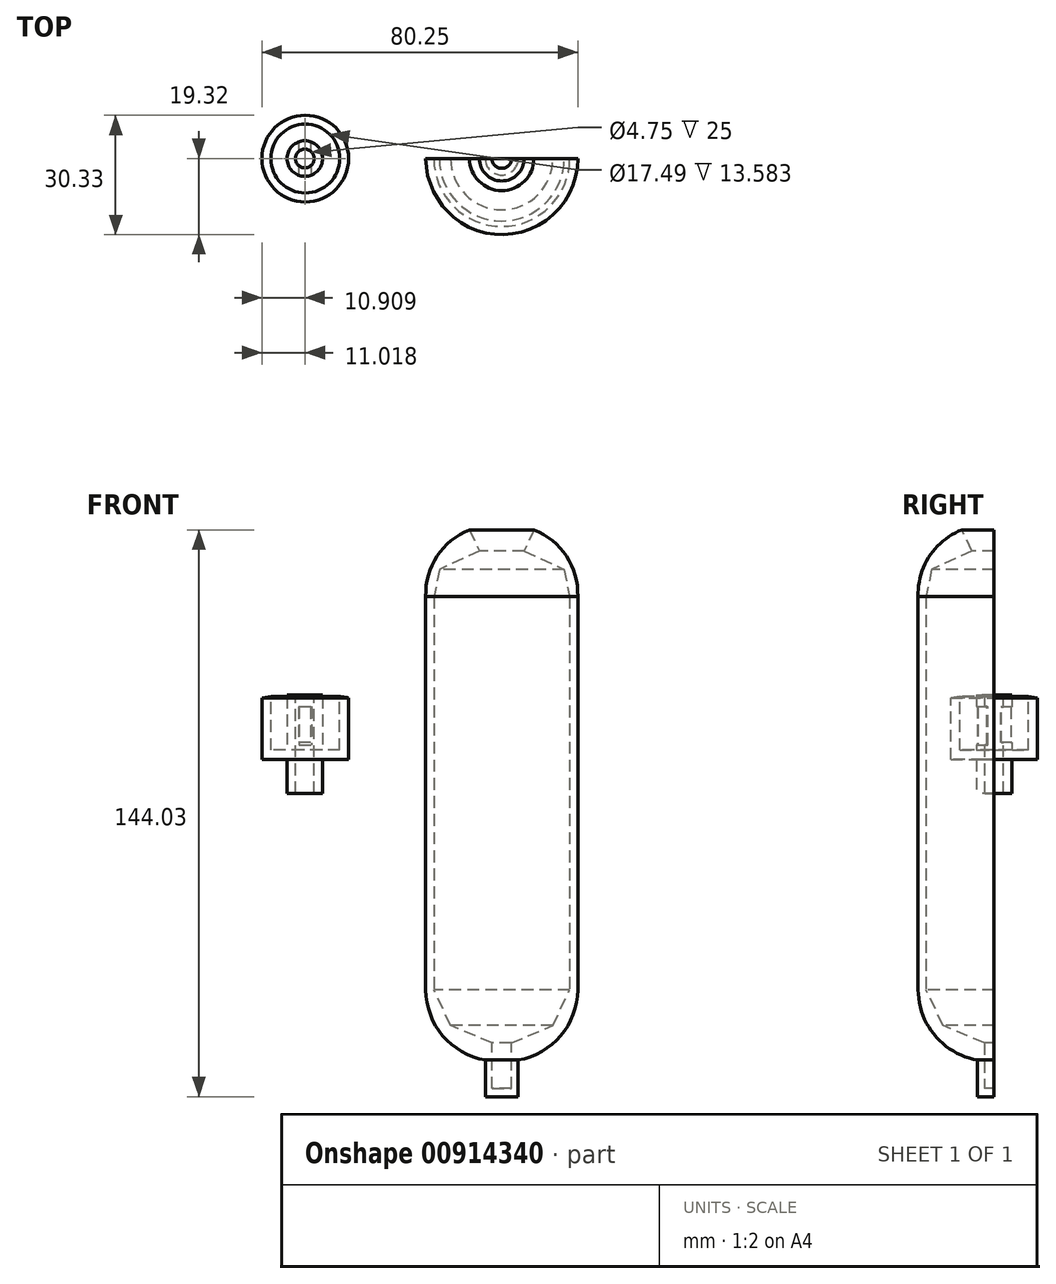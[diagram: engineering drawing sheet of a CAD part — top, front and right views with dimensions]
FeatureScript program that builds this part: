
annotation { "Feature Type Name" : "Feature", "Feature Type Description" : "" }
export const myFeature = defineFeature(function(context is Context, id is Id, definition is map)
    precondition{}
    {
        {
            var Q0;
            Q0=qCreatedBy(makeId("Front.planeOp"),FACE);
            var sketch = newSketch(context, id + "F0", { "sketchPlane" : qUnion([Q0])});
            skLineSegment(sketch, "E0", {"start": v(0, 0) * mm, "end": v(0, 50) * mm});
            skArc(sketch, "E1", {"start": v(0, 50) * mm, "mid": v(2.88, 60.25) * mm, "end": v(11.14, 66.96) * mm});
            skLineSegment(sketch, "E2", {"start": v(11.14, 66.96) * mm, "end": v(13.62, 61.6) * mm});
            skLineSegment(sketch, "E3", {"start": v(13.62, 61.6) * mm, "end": v(3.44, 56.9) * mm});
            skLineSegment(sketch, "E4", {"start": v(3.44, 56.9) * mm, "end": v(2.06, 49.9) * mm});
            skLineSegment(sketch, "E5", {"start": v(2.06, 49.9) * mm, "end": v(2.06, -49.9) * mm});
            skLineSegment(sketch, "E6", {"start": v(0, 0) * mm, "end": v(0, -49.9) * mm});
            skArc(sketch, "E7", {"start": v(0, -49.9) * mm, "mid": v(4.32, -61.58) * mm, "end": v(15.12, -67.77) * mm});
            skLineSegment(sketch, "E8", {"start": v(15.12, -67.77) * mm, "end": v(15.12, -77.07) * mm});
            skLineSegment(sketch, "E9", {"start": v(15.12, -77.07) * mm, "end": v(19.3, -77.07) * mm});
            skLineSegment(sketch, "E10", {"start": v(19.3, -77.07) * mm, "end": v(19.3, -75) * mm});
            skLineSegment(sketch, "E11", {"start": v(19.3, -75) * mm, "end": v(16.82, -75) * mm});
            skLineSegment(sketch, "E12", {"start": v(16.82, -75) * mm, "end": v(16.82, -67.77) * mm});
            skLineSegment(sketch, "E13", {"start": v(16.82, -67.77) * mm, "end": v(16.82, -63.39) * mm});
            skLineSegment(sketch, "E14", {"start": v(16.82, -63.39) * mm, "end": v(6.32, -58.97) * mm});
            skLineSegment(sketch, "E15", {"start": v(6.32, -58.97) * mm, "end": v(2.06, -49.9) * mm});
            skSolve(sketch);
        }
        {
            var Q0;
            Q0=makeQuery(id+"F0.imprint","IMPRINT",FACE,{"disambiguationData":[TD([[makeQuery(id+"F0.imprint","IMPRINT",EDGE,{"derivedFrom":sQuery(id+"F0.wireOp",EDGE,"E0")}),-1.0]])]});
            var Q1;
            Q1=sQuery(id+"F0.wireOp",EDGE,"E10");
            revolve(context, id + "F1", {"surfaceOperationType" : NewSurfaceOperationType.NEW, "entities" : qUnion([Q0]), "axis" : qUnion([Q1]), "revolveType" : RevolveType.ONE_DIRECTION, "angle" : 180 * degree});
        }
        {
            var Q0;
            Q0=qCreatedBy(makeId("Front.planeOp"),FACE);
            var sketch = newSketch(context, id + "F2", { "sketchPlane" : qUnion([Q0])});
            skLineSegment(sketch, "E16", {"start": v(-19.59, 24.26) * mm, "end": v(-19.59, 8.55) * mm});
            skLineSegment(sketch, "E17", {"start": v(-19.59, 8.55) * mm, "end": v(-30.6, 8.55) * mm});
            skLineSegment(sketch, "E18", {"start": v(-30.6, 8.55) * mm, "end": v(-30.6, 11) * mm});
            skLineSegment(sketch, "E19", {"start": v(-30.6, 11) * mm, "end": v(-21.86, 11) * mm});
            skLineSegment(sketch, "E20", {"start": v(-21.86, 11) * mm, "end": v(-21.86, 24.59) * mm});
            skLineSegment(sketch, "E21", {"start": v(-21.86, 24.59) * mm, "end": v(-19.59, 24.26) * mm});
            skSolve(sketch);
        }
        {
            var Q0;
            Q0=makeQuery(id+"F2.imprint","IMPRINT",FACE,{"disambiguationData":[TD([[makeQuery(id+"F2.imprint","IMPRINT",EDGE,{"derivedFrom":sQuery(id+"F2.wireOp",EDGE,"E16")}),-1.0]])]});
            var Q1;
            Q1=sQuery(id+"F2.wireOp",EDGE,"E18");
            revolve(context, id + "F3", {"surfaceOperationType" : NewSurfaceOperationType.NEW, "entities" : qUnion([Q0]), "axis" : qUnion([Q1]), "revolveType" : RevolveType.ONE_DIRECTION, "oppositeDirection" : true, "angle" : 360 * degree});
        }
        {
            var Q0;
            Q0=qCreatedBy(makeId("Top.planeOp"),FACE);
            var sketch = newSketch(context, id + "F4", { "sketchPlane" : qUnion([Q0])});
            skCircle(sketch, "E22", {"center": v(-30.71, 0) * mm, "radius": 4.52 * mm});
            skSolve(sketch);
        }
        {
            var Q0;
            Q0=makeQuery(id+"F4.imprint","IMPRINT",FACE,{"disambiguationData":[TD([[makeQuery(id+"F4.imprint","IMPRINT",EDGE,{"derivedFrom":sQuery(id+"F4.wireOp",EDGE,"E22")}),1.0]])]});
            extrude(context, id + "F5", {"entities" : qUnion([Q0]), "operationType" : NewBodyOperationType.ADD, "depth" : 25 * mm, "offsetDistance" : 25 * mm});
        }
        {
            var Q0;
            Q0=makeQuery(id+"F5.opExtrude","CAP_FACE",FACE,{"disambiguationData":[OSD([sQuery(id+"F4.wireOp",EDGE,"E22")])],"isStart":false});
            var sketch = newSketch(context, id + "F6", { "sketchPlane" : qUnion([Q0])});
            skCircle(sketch, "E23", {"center": v(-30.71, 0) * mm, "radius": 2.37 * mm});
            skSolve(sketch);
        }
        {
            var Q0;
            Q0=makeQuery(id+"F6.imprint","IMPRINT",FACE,{"disambiguationData":[TD([[makeQuery(id+"F6.imprint","IMPRINT",EDGE,{"derivedFrom":sQuery(id+"F6.wireOp",EDGE,"E23")}),1.0]])]});
            var Q1;
            Q1=sQuery(id+"F6.wireOp",EDGE,"E23");
            extrude(context, id + "F7", {"entities" : qUnion([Q0]), "operationType" : NewBodyOperationType.REMOVE, "surfaceEntities" : qUnion([Q1]), "oppositeDirection" : true, "depth" : 25 * mm, "offsetDistance" : 25 * mm});
        }
        {
            var Q0;
            Q0=qCreatedBy(makeId("Front.planeOp"),FACE);
            var sketch = newSketch(context, id + "F8", { "sketchPlane" : qUnion([Q0])});
            skLineSegment(sketch, "E24.bottom", {"start": v(-32.19, 22.05) * mm, "end": v(-28.97, 22.05) * mm});
            skLineSegment(sketch, "E24.top", {"start": v(-32.19, 12.3) * mm, "end": v(-28.97, 12.3) * mm});
            skLineSegment(sketch, "E24.left", {"start": v(-32.19, 22.05) * mm, "end": v(-32.19, 12.3) * mm});
            skLineSegment(sketch, "E24.right", {"start": v(-28.97, 22.05) * mm, "end": v(-28.97, 12.3) * mm});
            skSolve(sketch);
        }
        {
            var Q0;
            Q0 = qSketchRegion(id + "F8", true);
            extrude(context, id + "F9", {"entities" : qUnion([Q0]), "operationType" : NewBodyOperationType.REMOVE, "depth" : 6 * mm, "offsetDistance" : 25 * mm});
        }
        {
            var Q0;
            Q0=qCreatedBy(makeId("Front.planeOp"),FACE);
            var sketch = newSketch(context, id + "F10", { "sketchPlane" : qUnion([Q0])});
            skLineSegment(sketch, "E25.bottom", {"start": v(-29.3, 21.9) * mm, "end": v(-32.28, 21.9) * mm});
            skLineSegment(sketch, "E25.top", {"start": v(-29.3, 12.9) * mm, "end": v(-32.28, 12.9) * mm});
            skLineSegment(sketch, "E25.left", {"start": v(-29.3, 21.9) * mm, "end": v(-29.3, 12.9) * mm});
            skLineSegment(sketch, "E25.right", {"start": v(-32.28, 21.9) * mm, "end": v(-32.28, 12.9) * mm});
            skSolve(sketch);
        }
        {
            var Q0;
            Q0 = qSketchRegion(id + "F10", true);
            extrude(context, id + "F11", {"entities" : qUnion([Q0]), "operationType" : NewBodyOperationType.REMOVE, "oppositeDirection" : true, "depth" : 6 * mm, "offsetDistance" : 25 * mm});
        }
    });
